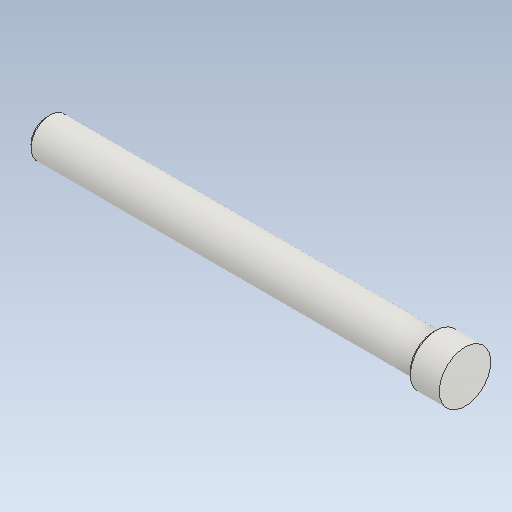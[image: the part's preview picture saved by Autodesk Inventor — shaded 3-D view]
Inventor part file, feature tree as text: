
AUTODESK INVENTOR PART (.ipt)
format: ipt  version: 2020 (Build 240168000, 168)  size: 100,352 bytes
history: native  units: in
note: dims shown in document units (in); Inventor stores cm internally (conversion verified against a paired STEP export)
features: other x9, plane x1
ambient origin geometry x8: Origin, YZ Plane, XZ Plane, XY Plane, X Axis, Y Axis, Z Axis, Center Point
bodies: Solid1 (feature_tree)
feature tree (10):
  other  "Shaft"
  other  "Solid1::Shaft"
  other  "TaggingFeature1"
  other  "Main Sketch"
  other  "Start Plane"
  plane  "XY Plane_1"
  other  "X Axis_1"
  other  "Axial Mate"
  other  "Start plane Mate"
  other  "Orientation plane Mate"
